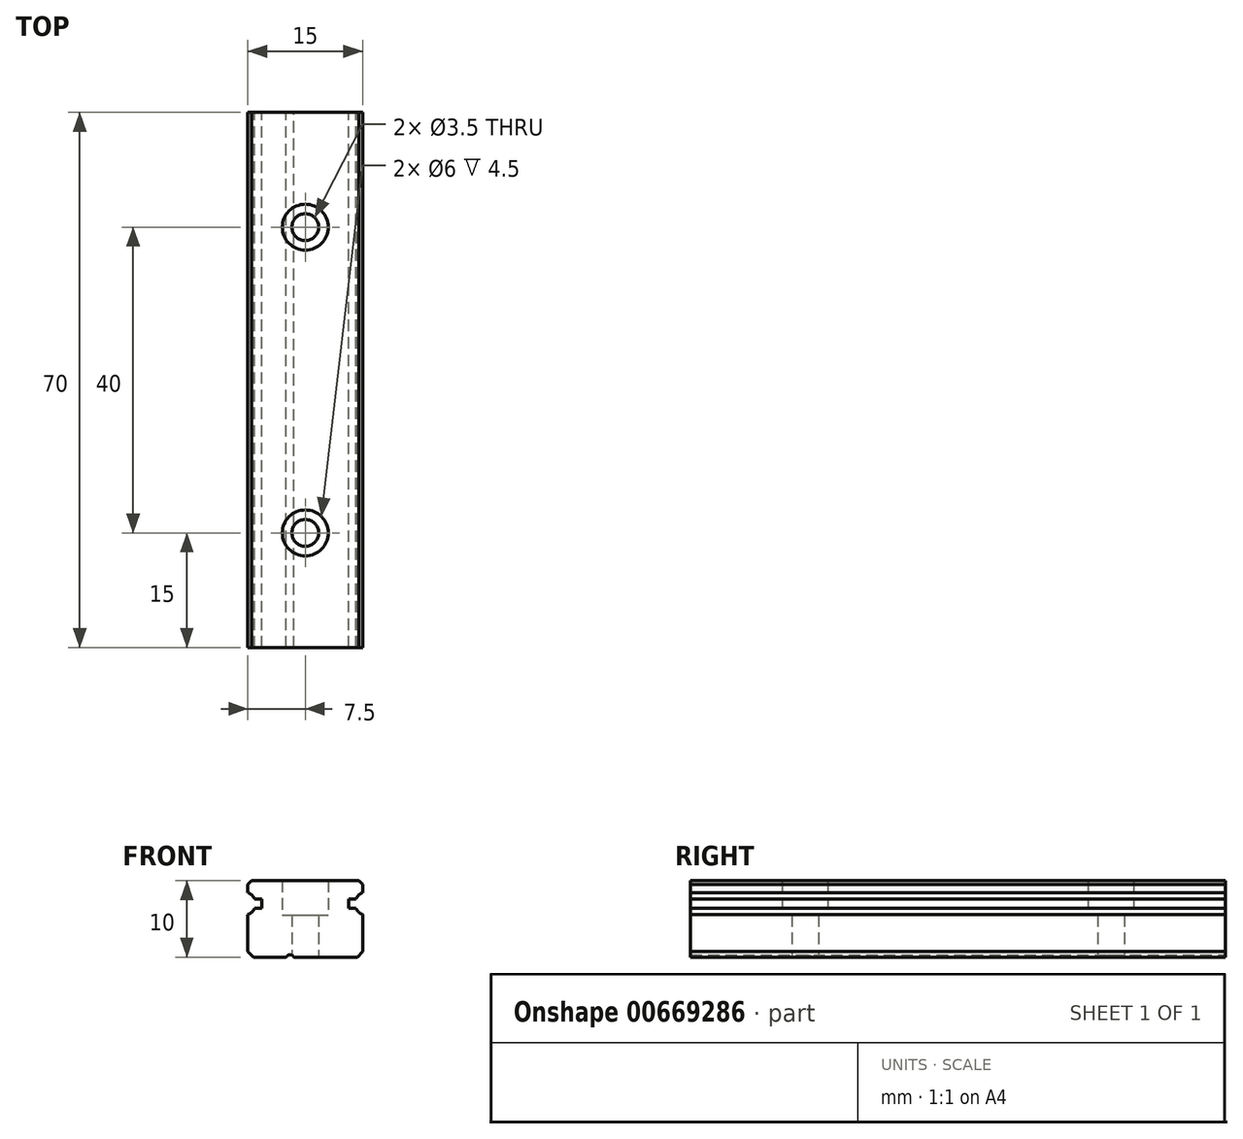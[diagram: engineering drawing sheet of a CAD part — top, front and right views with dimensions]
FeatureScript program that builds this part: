
annotation { "Feature Type Name" : "Feature", "Feature Type Description" : "" }
export const myFeature = defineFeature(function(context is Context, id is Id, definition is map)
    precondition{}
    {
        {
            var Q0;
            Q0=qCreatedBy(makeId("Front.planeOp"),FACE);
            var sketch = newSketch(context, id + "F0", { "sketchPlane" : qUnion([Q0])});
            skPoint(sketch, "E0.middle", {"position": v(0, 0) * mm});
            skLineSegment(sketch, "E1.bottom", {"start": v(6.8, -5) * mm, "end": v(-1.51, -5) * mm});
            skLineSegment(sketch, "E1.top", {"start": v(7, 5) * mm, "end": v(-7, 5) * mm});
            skLineSegment(sketch, "E1.left", {"start": v(7.5, -4.3) * mm, "end": v(7.5, 0.59) * mm});
            skLineSegment(sketch, "E1.right", {"start": v(-7.5, -4.3) * mm, "end": v(-7.5, 0.59) * mm});
            skArc(sketch, "E2", {"start": v(-7.5, 0.59) * mm, "mid": v(-6.98, 0.9) * mm, "end": v(-6.63, 1.4) * mm});
            skArc(sketch, "E3", {"start": v(7.5, 3.41) * mm, "mid": v(6.98, 3.1) * mm, "end": v(6.63, 2.6) * mm});
            skLineSegment(sketch, "E4", {"start": v(5.7, 2.6) * mm, "end": v(6.63, 2.6) * mm});
            skLineSegment(sketch, "E5", {"start": v(5.7, 1.4) * mm, "end": v(6.63, 1.4) * mm});
            skLineSegment(sketch, "E6", {"start": v(-5.7, 1.4) * mm, "end": v(-6.63, 1.4) * mm});
            skLineSegment(sketch, "E7", {"start": v(-5.7, 2.6) * mm, "end": v(-6.63, 2.6) * mm});
            skLineSegment(sketch, "E8", {"start": v(-7.5, 4.5) * mm, "end": v(-7, 5) * mm});
            skLineSegment(sketch, "E9.MirrorCS", {"start": v(7.5, 4.5) * mm, "end": v(7, 5) * mm});
            skLineSegment(sketch, "E10.MirrorCS", {"start": v(7.5, -4.3) * mm, "end": v(6.8, -5) * mm});
            skLineSegment(sketch, "E11.MirrorCS", {"start": v(-7.5, -4.3) * mm, "end": v(-6.8, -5) * mm});
            skPoint(sketch, "E12.orphan", {"position": v(-7.5, 5) * mm});
            skLineSegment(sketch, "E13.trimOffspring", {"start": v(-7.5, 3.41) * mm, "end": v(-7.5, 4.5) * mm});
            skArc(sketch, "E14.trimOffspring", {"start": v(-6.63, 2.6) * mm, "mid": v(-6.98, 3.1) * mm, "end": v(-7.5, 3.41) * mm});
            skPoint(sketch, "E15.orphan", {"position": v(7.5, 5) * mm});
            skLineSegment(sketch, "E16.trimOffspring", {"start": v(7.5, 3.41) * mm, "end": v(7.5, 4.5) * mm});
            skArc(sketch, "E17.trimOffspring", {"start": v(6.63, 1.4) * mm, "mid": v(6.98, 0.9) * mm, "end": v(7.5, 0.59) * mm});
            skPoint(sketch, "E18.orphan", {"position": v(7.5, -5) * mm});
            skPoint(sketch, "E19.orphan", {"position": v(-7.5, -5) * mm});
            skLineSegment(sketch, "E20", {"start": v(-5.7, 2.6) * mm, "end": v(-5.7, 1.4) * mm});
            skLineSegment(sketch, "E21", {"start": v(5.7, 2.6) * mm, "end": v(5.7, 1.4) * mm});
            skLineSegment(sketch, "E22", {"start": v(-8, 2) * mm, "end": v(8, 2) * mm, "construction": true});
            skArc(sketch, "E23", {"start": v(-1.51, -5) * mm, "mid": v(-2, -4.7) * mm, "end": v(-2.49, -5) * mm});
            skLineSegment(sketch, "E24.trimOffspring", {"start": v(-2.49, -5) * mm, "end": v(-6.8, -5) * mm});
            skLineSegment(sketch, "E25", {"start": v(-2.49, -5) * mm, "end": v(-1.51, -5) * mm, "construction": true});
            skSolve(sketch);
        }
        {
            var Q0;
            Q0=makeQuery(id+"F0.imprint","IMPRINT",FACE,{"disambiguationData":[TD([[makeQuery(id+"F0.imprint","IMPRINT",EDGE,{"derivedFrom":sQuery(id+"F0.wireOp",EDGE,"E1.bottom")}),-1.0]])]});
            extrude(context, id + "F1", {"entities" : qUnion([Q0]), "depth" : 70 * mm, "offsetDistance" : 25 * mm});
        }
        {
            var Q0;
            Q0=makeQuery(id+"F1.opExtrude","SWEPT_FACE",FACE,{"disambiguationData":[OSD([sQuery(id+"F0.wireOp",EDGE,"E1.top")])]});
            var sketch = newSketch(context, id + "F2", { "sketchPlane" : qUnion([Q0])});
            skPoint(sketch, "E26", {"position": v(0, -15) * mm});
            skPoint(sketch, "E27.0.1.0", {"position": v(0, -55) * mm});
            skPoint(sketch, "E27.0.2.0", {"position": v(0, -95) * mm});
            skPoint(sketch, "E27.0.3.0", {"position": v(0, -135) * mm});
            skPoint(sketch, "E27.0.4.0", {"position": v(0, -175) * mm});
            skPoint(sketch, "E27.0.5.0", {"position": v(0, -215) * mm});
            skPoint(sketch, "E27.0.6.0", {"position": v(0, -255) * mm});
            skPoint(sketch, "E27.0.7.0", {"position": v(0, -295) * mm});
            skPoint(sketch, "E27.0.8.0", {"position": v(0, -335) * mm});
            skPoint(sketch, "E27.0.9.0", {"position": v(0, -375) * mm});
            skPoint(sketch, "E27.0.10.0", {"position": v(0, -415) * mm});
            skPoint(sketch, "E27.0.11.0", {"position": v(0, -455) * mm});
            skPoint(sketch, "E27.0.12.0", {"position": v(0, -495) * mm});
            skPoint(sketch, "E27.0.13.0", {"position": v(0, -535) * mm});
            skPoint(sketch, "E27.0.14.0", {"position": v(0, -575) * mm});
            skPoint(sketch, "E27.0.15.0", {"position": v(0, -615) * mm});
            skPoint(sketch, "E27.0.16.0", {"position": v(0, -655) * mm});
            skPoint(sketch, "E27.0.17.0", {"position": v(0, -695) * mm});
            skPoint(sketch, "E27.0.18.0", {"position": v(0, -735) * mm});
            skPoint(sketch, "E27.0.19.0", {"position": v(0, -775) * mm});
            skPoint(sketch, "E27.0.20.0", {"position": v(0, -815) * mm});
            skPoint(sketch, "E27.0.21.0", {"position": v(0, -855) * mm});
            skPoint(sketch, "E27.0.22.0", {"position": v(0, -895) * mm});
            skPoint(sketch, "E27.0.23.0", {"position": v(0, -935) * mm});
            skPoint(sketch, "E27.0.24.0", {"position": v(0, -975) * mm});
            skPoint(sketch, "E27.0.25.0", {"position": v(0, -1015) * mm});
            skPoint(sketch, "E27.0.26.0", {"position": v(0, -1055) * mm});
            skPoint(sketch, "E27.0.27.0", {"position": v(0, -1095) * mm});
            skPoint(sketch, "E27.0.28.0", {"position": v(0, -1135) * mm});
            skPoint(sketch, "E27.0.29.0", {"position": v(0, -1175) * mm});
            skPoint(sketch, "E27.0.30.0", {"position": v(0, -1215) * mm});
            skPoint(sketch, "E27.0.31.0", {"position": v(0, -1255) * mm});
            skPoint(sketch, "E27.0.32.0", {"position": v(0, -1295) * mm});
            skPoint(sketch, "E27.0.33.0", {"position": v(0, -1335) * mm});
            skPoint(sketch, "E27.0.34.0", {"position": v(0, -1375) * mm});
            skPoint(sketch, "E27.0.35.0", {"position": v(0, -1415) * mm});
            skPoint(sketch, "E27.0.36.0", {"position": v(0, -1455) * mm});
            skPoint(sketch, "E27.0.37.0", {"position": v(0, -1495) * mm});
            skPoint(sketch, "E27.0.38.0", {"position": v(0, -1535) * mm});
            skPoint(sketch, "E27.0.39.0", {"position": v(0, -1575) * mm});
            skPoint(sketch, "E27.0.40.0", {"position": v(0, -1615) * mm});
            skPoint(sketch, "E27.0.41.0", {"position": v(0, -1655) * mm});
            skPoint(sketch, "E27.0.42.0", {"position": v(0, -1695) * mm});
            skPoint(sketch, "E27.0.43.0", {"position": v(0, -1735) * mm});
            skPoint(sketch, "E27.0.44.0", {"position": v(0, -1775) * mm});
            skPoint(sketch, "E27.0.45.0", {"position": v(0, -1815) * mm});
            skPoint(sketch, "E27.0.46.0", {"position": v(0, -1855) * mm});
            skPoint(sketch, "E27.0.47.0", {"position": v(0, -1895) * mm});
            skPoint(sketch, "E27.0.48.0", {"position": v(0, -1935) * mm});
            skPoint(sketch, "E27.0.49.0", {"position": v(0, -1975) * mm});
            skLineSegment(sketch, "E27.direction2", {"start": v(0, -15) * mm, "end": v(0, -55) * mm, "construction": true});
            skSolve(sketch);
        }
        {
            var Q0;
            Q0=sQuery(id+"F2.wireOp",VERTEX,"E27.0.2.0");
            var Q1;
            Q1=sQuery(id+"F2.wireOp",VERTEX,"E27.0.5.0");
            var Q2;
            Q2=sQuery(id+"F2.wireOp",VERTEX,"E27.0.7.0");
            var Q3;
            Q3=sQuery(id+"F2.wireOp",VERTEX,"E27.0.1.0");
            var Q4;
            Q4=sQuery(id+"F2.wireOp",VERTEX,"E27.0.8.0");
            var Q5;
            Q5=sQuery(id+"F2.wireOp",VERTEX,"E26");
            var Q6;
            Q6=sQuery(id+"F2.wireOp",VERTEX,"E27.0.4.0");
            var Q7;
            Q7=sQuery(id+"F2.wireOp",VERTEX,"E27.0.6.0");
            var Q8;
            Q8=sQuery(id+"F2.wireOp",VERTEX,"E27.0.3.0");
            var Q9;
            Q9=sQuery(id+"F2.wireOp",VERTEX,"E27.0.21.0");
            var Q10;
            Q10=sQuery(id+"F2.wireOp",VERTEX,"E27.0.11.0");
            var Q11;
            Q11=sQuery(id+"F2.wireOp",VERTEX,"E27.0.22.0");
            var Q12;
            Q12=sQuery(id+"F2.wireOp",VERTEX,"E27.0.20.0");
            var Q13;
            Q13=sQuery(id+"F2.wireOp",VERTEX,"E27.0.16.0");
            var Q14;
            Q14=sQuery(id+"F2.wireOp",VERTEX,"E27.0.19.0");
            var Q15;
            Q15=sQuery(id+"F2.wireOp",VERTEX,"E27.0.23.0");
            var Q16;
            Q16=sQuery(id+"F2.wireOp",VERTEX,"E27.0.15.0");
            var Q17;
            Q17=sQuery(id+"F2.wireOp",VERTEX,"E27.0.18.0");
            var Q18;
            Q18=sQuery(id+"F2.wireOp",VERTEX,"E27.0.13.0");
            var Q19;
            Q19=sQuery(id+"F2.wireOp",VERTEX,"E27.0.17.0");
            var Q20;
            Q20=sQuery(id+"F2.wireOp",VERTEX,"E27.0.9.0");
            var Q21;
            Q21=sQuery(id+"F2.wireOp",VERTEX,"E27.0.14.0");
            var Q22;
            Q22=sQuery(id+"F2.wireOp",VERTEX,"E27.0.12.0");
            var Q23;
            Q23=sQuery(id+"F2.wireOp",VERTEX,"E27.0.10.0");
            var Q24;
            Q24=sQuery(id+"F2.wireOp",VERTEX,"E27.0.29.0");
            var Q25;
            Q25=sQuery(id+"F2.wireOp",VERTEX,"E27.0.34.0");
            var Q26;
            Q26=sQuery(id+"F2.wireOp",VERTEX,"E27.0.30.0");
            var Q27;
            Q27=sQuery(id+"F2.wireOp",VERTEX,"E27.0.40.0");
            var Q28;
            Q28=sQuery(id+"F2.wireOp",VERTEX,"E27.0.27.0");
            var Q29;
            Q29=sQuery(id+"F2.wireOp",VERTEX,"E27.0.28.0");
            var Q30;
            Q30=sQuery(id+"F2.wireOp",VERTEX,"E27.0.41.0");
            var Q31;
            Q31=sQuery(id+"F2.wireOp",VERTEX,"E27.0.31.0");
            var Q32;
            Q32=sQuery(id+"F2.wireOp",VERTEX,"E27.0.26.0");
            var Q33;
            Q33=sQuery(id+"F2.wireOp",VERTEX,"E27.0.32.0");
            var Q34;
            Q34=sQuery(id+"F2.wireOp",VERTEX,"E27.0.24.0");
            var Q35;
            Q35=sQuery(id+"F2.wireOp",VERTEX,"E27.0.38.0");
            var Q36;
            Q36=sQuery(id+"F2.wireOp",VERTEX,"E27.0.35.0");
            var Q37;
            Q37=sQuery(id+"F2.wireOp",VERTEX,"E27.0.42.0");
            var Q38;
            Q38=sQuery(id+"F2.wireOp",VERTEX,"E27.0.33.0");
            var Q39;
            Q39=sQuery(id+"F2.wireOp",VERTEX,"E27.0.39.0");
            var Q40;
            Q40=sQuery(id+"F2.wireOp",VERTEX,"E27.0.37.0");
            var Q41;
            Q41=sQuery(id+"F2.wireOp",VERTEX,"E27.0.25.0");
            var Q42;
            Q42=sQuery(id+"F2.wireOp",VERTEX,"E27.0.36.0");
            var Q43;
            Q43=sQuery(id+"F2.wireOp",VERTEX,"E27.0.47.0");
            var Q44;
            Q44=sQuery(id+"F2.wireOp",VERTEX,"E27.0.44.0");
            var Q45;
            Q45=sQuery(id+"F2.wireOp",VERTEX,"E27.0.43.0");
            var Q46;
            Q46=sQuery(id+"F2.wireOp",VERTEX,"E27.0.49.0");
            var Q47;
            Q47=sQuery(id+"F2.wireOp",VERTEX,"E27.0.48.0");
            var Q48;
            Q48=sQuery(id+"F2.wireOp",VERTEX,"E27.0.45.0");
            var Q49;
            Q49=sQuery(id+"F2.wireOp",VERTEX,"E27.0.46.0");
            var Q50;
            Q50=makeQuery(id+"F1.opExtrude","SWEPT_BODY",BODY,{"disambiguationData":[OSD([sQuery(id+"F0.wireOp",EDGE,"E1.bottom"),sQuery(id+"F0.wireOp",EDGE,"E1.top"),sQuery(id+"F0.wireOp",EDGE,"E1.left"),sQuery(id+"F0.wireOp",EDGE,"E1.right"),sQuery(id+"F0.wireOp",EDGE,"E2"),sQuery(id+"F0.wireOp",EDGE,"E3"),sQuery(id+"F0.wireOp",EDGE,"E4"),sQuery(id+"F0.wireOp",EDGE,"E5"),sQuery(id+"F0.wireOp",EDGE,"E6"),sQuery(id+"F0.wireOp",EDGE,"E7"),sQuery(id+"F0.wireOp",EDGE,"E8"),sQuery(id+"F0.wireOp",EDGE,"E9.MirrorCS"),sQuery(id+"F0.wireOp",EDGE,"E10.MirrorCS"),sQuery(id+"F0.wireOp",EDGE,"E11.MirrorCS"),sQuery(id+"F0.wireOp",EDGE,"E13.trimOffspring"),sQuery(id+"F0.wireOp",EDGE,"E14.trimOffspring"),sQuery(id+"F0.wireOp",EDGE,"E16.trimOffspring"),sQuery(id+"F0.wireOp",EDGE,"E17.trimOffspring"),sQuery(id+"F0.wireOp",EDGE,"E20"),sQuery(id+"F0.wireOp",EDGE,"E21"),sQuery(id+"F0.wireOp",EDGE,"E23"),sQuery(id+"F0.wireOp",EDGE,"E24.trimOffspring")])]});
            hole(context, id + "F3", {"style" : HoleStyle.C_BORE, "endStyle" : HoleEndStyle.THROUGH, "holeDiameter" : 3.5 * mm, "cBoreDiameter" : 6 * mm, "cBoreDepth" : 4.5 * mm, "majorDiameter" : 5 * mm, "isTappedThrough" : true, "tappedDepth" : 12 * mm, "tapClearance" : 3, "locations" : qUnion([Q0, Q1, Q2, Q3, Q4, Q5, Q6, Q7, Q8, Q9, Q10, Q11, Q12, Q13, Q14, Q15, Q16, Q17, Q18, Q19, Q20, Q21, Q22, Q23, Q24, Q25, Q26, Q27, Q28, Q29, Q30, Q31, Q32, Q33, Q34, Q35, Q36, Q37, Q38, Q39, Q40, Q41, Q42, Q43, Q44, Q45, Q46, Q47, Q48, Q49]), "scope" : qUnion([Q50]), "startStyle" : HoleStartStyle.PART});
        }
    });
